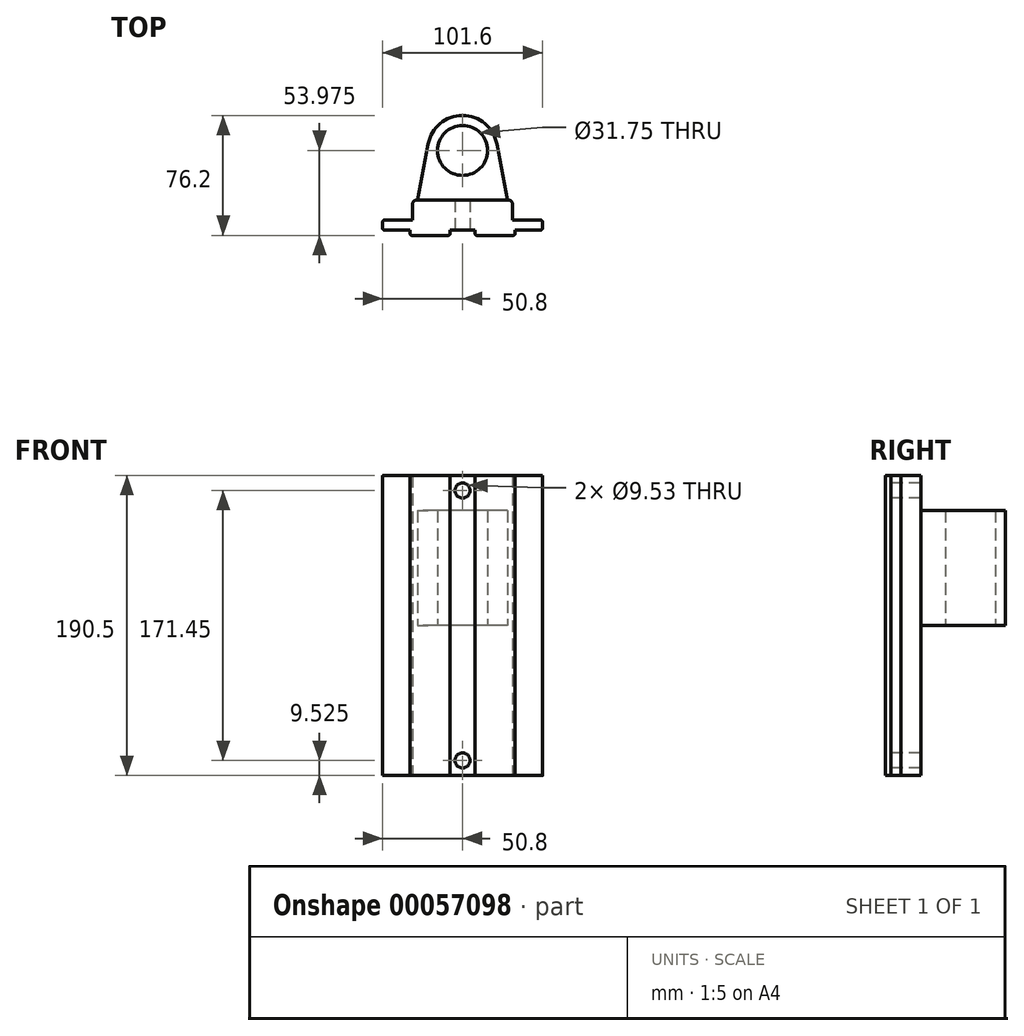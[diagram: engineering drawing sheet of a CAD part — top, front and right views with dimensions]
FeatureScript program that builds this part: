
annotation { "Feature Type Name" : "Feature", "Feature Type Description" : "" }
export const myFeature = defineFeature(function(context is Context, id is Id, definition is map)
    precondition{}
    {
        {
            var Q0;
            Q0=qCreatedBy(makeId("Top.planeOp"),FACE);
            var sketch = newSketch(context, id + "F0", { "sketchPlane" : qUnion([Q0])});
            skLineSegment(sketch, "E0", {"start": v(0, 0) * mm, "end": v(0, 22.42) * mm});
            skLineSegment(sketch, "E1", {"start": v(-9.2, 0) * mm, "end": v(-32.07, 0) * mm});
            skLineSegment(sketch, "E2", {"start": v(-50.8, 4.64) * mm, "end": v(-50.8, 8.45) * mm});
            skLineSegment(sketch, "E3", {"start": v(-49.53, 3.37) * mm, "end": v(0, 3.37) * mm});
            skLineSegment(sketch, "E4", {"start": v(-49.53, 9.72) * mm, "end": v(0, 9.72) * mm});
            skLineSegment(sketch, "E5", {"start": v(-33.34, 3.37) * mm, "end": v(-33.34, 1.27) * mm});
            skLineSegment(sketch, "E6", {"start": v(-7.94, 1.27) * mm, "end": v(-7.94, 3.37) * mm});
            skLineSegment(sketch, "E7", {"start": v(0, 22.42) * mm, "end": v(-29.21, 22.42) * mm});
            skLineSegment(sketch, "E8", {"start": v(-31.75, 19.88) * mm, "end": v(-31.75, 9.72) * mm});
            skPoint(sketch, "E9.visualSharp", {"position": v(-31.75, 22.42) * mm});
            skArc(sketch, "E9.filletArc", {"start": v(-29.21, 22.42) * mm, "mid": v(-31, 21.68) * mm, "end": v(-31.75, 19.88) * mm});
            skPoint(sketch, "E10.visualSharp", {"position": v(-50.8, 9.72) * mm});
            skArc(sketch, "E10.filletArc", {"start": v(-49.53, 9.72) * mm, "mid": v(-50.43, 9.35) * mm, "end": v(-50.8, 8.45) * mm});
            skPoint(sketch, "E11.visualSharp", {"position": v(-50.8, 3.37) * mm});
            skArc(sketch, "E11.filletArc", {"start": v(-50.8, 4.64) * mm, "mid": v(-50.43, 3.75) * mm, "end": v(-49.53, 3.37) * mm});
            skPoint(sketch, "E12.visualSharp", {"position": v(-33.34, 0) * mm});
            skArc(sketch, "E12.filletArc", {"start": v(-33.34, 1.27) * mm, "mid": v(-32.97, 0.37) * mm, "end": v(-32.07, 0) * mm});
            skPoint(sketch, "E13.visualSharp", {"position": v(-7.94, 0) * mm});
            skArc(sketch, "E13.filletArc", {"start": v(-9.2, 0) * mm, "mid": v(-8.3, 0.37) * mm, "end": v(-7.94, 1.27) * mm});
            skPoint(sketch, "E14.orphan", {"position": v(-26.99, 22.42) * mm});
            skArc(sketch, "E15.MirrorCS", {"start": v(49.53, 9.72) * mm, "mid": v(50.43, 9.35) * mm, "end": v(50.8, 8.45) * mm});
            skArc(sketch, "E16.MirrorCS", {"start": v(50.8, 4.64) * mm, "mid": v(50.43, 3.75) * mm, "end": v(49.53, 3.37) * mm});
            skLineSegment(sketch, "E17.MirrorCS", {"start": v(50.8, 4.64) * mm, "end": v(50.8, 8.45) * mm});
            skArc(sketch, "E18.MirrorCS", {"start": v(29.21, 22.42) * mm, "mid": v(31, 21.68) * mm, "end": v(31.75, 19.88) * mm});
            skArc(sketch, "E19.MirrorCS", {"start": v(33.34, 1.27) * mm, "mid": v(32.97, 0.37) * mm, "end": v(32.07, 0) * mm});
            skArc(sketch, "E20.MirrorCS", {"start": v(9.2, 0) * mm, "mid": v(8.3, 0.37) * mm, "end": v(7.94, 1.27) * mm});
            skLineSegment(sketch, "E21.MirrorCS", {"start": v(33.34, 3.37) * mm, "end": v(33.34, 1.27) * mm});
            skLineSegment(sketch, "E22.MirrorCS", {"start": v(7.94, 1.27) * mm, "end": v(7.94, 3.37) * mm});
            skPoint(sketch, "E23.MirrorP", {"position": v(50.8, 3.37) * mm});
            skLineSegment(sketch, "E24.MirrorCS", {"start": v(9.2, 0) * mm, "end": v(32.07, 0) * mm});
            skLineSegment(sketch, "E25.MirrorCS", {"start": v(49.53, 3.37) * mm, "end": v(0, 3.37) * mm});
            skLineSegment(sketch, "E26.MirrorCS", {"start": v(49.53, 9.72) * mm, "end": v(0, 9.72) * mm});
            skLineSegment(sketch, "E27.MirrorCS", {"start": v(0, 22.42) * mm, "end": v(29.21, 22.42) * mm});
            skLineSegment(sketch, "E28.MirrorCS", {"start": v(31.75, 19.88) * mm, "end": v(31.75, 9.72) * mm});
            skPoint(sketch, "E29.MirrorP", {"position": v(7.94, 0) * mm});
            skPoint(sketch, "E30.MirrorP", {"position": v(50.8, 9.72) * mm});
            skPoint(sketch, "E31.MirrorP", {"position": v(33.34, 0) * mm});
            skPoint(sketch, "E32.MirrorP", {"position": v(26.99, 22.42) * mm});
            skPoint(sketch, "E33.MirrorP", {"position": v(31.75, 22.42) * mm});
            skSolve(sketch);
        }
        {
            var Q0;
            Q0 = qSketchRegion(id + "F0", true);
            extrude(context, id + "F1", {"entities" : qUnion([Q0]), "depth" : 190.5 * mm});
        }
        {
            var Q0;
            Q0=qCreatedBy(makeId("Top.planeOp"),FACE);
            cPlane(context, id + "F2", {"entities" : qUnion([Q0]), "cplaneType" : CPlaneType.OFFSET, "offset" : 95.25 * mm, "width" : 152.4 * mm, "height" : 152.4 * mm});
        }
        {
            var Q0;
            Q0=qCreatedBy(id+"F2.planeOp",FACE);
            var sketch = newSketch(context, id + "F3", { "sketchPlane" : qUnion([Q0])});
            skLineSegment(sketch, "E34", {"start": v(-28.58, 22.22) * mm, "end": v(-21.84, 58.08) * mm});
            skLineSegment(sketch, "E35", {"start": v(0, 22.22) * mm, "end": v(0, 38.1) * mm});
            skPoint(sketch, "E36", {"position": v(-22.22, 53.98) * mm});
            skArc(sketch, "E37", {"start": v(0, 69.85) * mm, "mid": v(-15.88, 53.98) * mm, "end": v(0, 38.1) * mm});
            skArc(sketch, "E38", {"start": v(0, 76.2) * mm, "mid": v(-22.23, 53.98) * mm, "end": v(0, 31.75) * mm});
            skLineSegment(sketch, "E39", {"start": v(0, 76.2) * mm, "end": v(0, 69.85) * mm});
            skLineSegment(sketch, "E40", {"start": v(-28.58, 22.22) * mm, "end": v(0, 22.22) * mm});
            skLineSegment(sketch, "E41", {"start": v(0, 69.85) * mm, "end": v(0, 76.2) * mm});
            skPoint(sketch, "E42.orphan", {"position": v(0, 0) * mm});
            skPoint(sketch, "E43.MirrorP", {"position": v(22.22, 53.98) * mm});
            skLineSegment(sketch, "E44.MirrorCS", {"start": v(28.58, 22.22) * mm, "end": v(21.84, 58.08) * mm});
            skLineSegment(sketch, "E45.MirrorCS", {"start": v(28.58, 22.22) * mm, "end": v(0, 22.22) * mm});
            skArc(sketch, "E46.MirrorCS", {"start": v(0, 76.2) * mm, "mid": v(22.23, 53.98) * mm, "end": v(0, 31.75) * mm});
            skArc(sketch, "E47.MirrorCS", {"start": v(0, 69.85) * mm, "mid": v(15.88, 53.98) * mm, "end": v(0, 38.1) * mm});
            skSolve(sketch);
        }
        {
            var Q0;
            Q0 = qSketchRegion(id + "F3", true);
            extrude(context, id + "F4", {"entities" : qUnion([Q0]), "operationType" : NewBodyOperationType.ADD, "depth" : 73.02 * mm});
        }
        {
            var Q0;
            Q0=qCreatedBy(makeId("Front.planeOp"),FACE);
            var sketch = newSketch(context, id + "F5", { "sketchPlane" : qUnion([Q0])});
            skLineSegment(sketch, "E48", {"start": v(0, 0) * mm, "end": v(0, 225.44) * mm, "construction": true});
            skPoint(sketch, "E49", {"position": v(0, 9.53) * mm});
            skPoint(sketch, "E50", {"position": v(0, 180.98) * mm});
            skSolve(sketch);
        }
        {
            var Q0;
            Q0=sQuery(id+"F5.wireOp",VERTEX,"E50");
            var Q1;
            Q1=makeQuery(id+"F1.opExtrude","SWEPT_BODY",BODY,{"disambiguationData":[OSD([sQuery(id+"F0.wireOp",EDGE,"E1"),sQuery(id+"F0.wireOp",EDGE,"E2"),sQuery(id+"F0.wireOp",EDGE,"E3"),sQuery(id+"F0.wireOp",EDGE,"E4"),sQuery(id+"F0.wireOp",EDGE,"E5"),sQuery(id+"F0.wireOp",EDGE,"E6"),sQuery(id+"F0.wireOp",EDGE,"E7"),sQuery(id+"F0.wireOp",EDGE,"E8"),sQuery(id+"F0.wireOp",EDGE,"E9.filletArc"),sQuery(id+"F0.wireOp",EDGE,"E10.filletArc"),sQuery(id+"F0.wireOp",EDGE,"E11.filletArc"),sQuery(id+"F0.wireOp",EDGE,"E12.filletArc"),sQuery(id+"F0.wireOp",EDGE,"E13.filletArc"),sQuery(id+"F0.wireOp",EDGE,"E15.MirrorCS"),sQuery(id+"F0.wireOp",EDGE,"E16.MirrorCS"),sQuery(id+"F0.wireOp",EDGE,"E17.MirrorCS"),sQuery(id+"F0.wireOp",EDGE,"E18.MirrorCS"),sQuery(id+"F0.wireOp",EDGE,"E19.MirrorCS"),sQuery(id+"F0.wireOp",EDGE,"E20.MirrorCS"),sQuery(id+"F0.wireOp",EDGE,"E21.MirrorCS"),sQuery(id+"F0.wireOp",EDGE,"E22.MirrorCS"),sQuery(id+"F0.wireOp",EDGE,"E24.MirrorCS"),sQuery(id+"F0.wireOp",EDGE,"E25.MirrorCS"),sQuery(id+"F0.wireOp",EDGE,"E26.MirrorCS"),sQuery(id+"F0.wireOp",EDGE,"E27.MirrorCS"),sQuery(id+"F0.wireOp",EDGE,"E28.MirrorCS")])]});
            hole(context, id + "F6", {"style" : HoleStyle.SIMPLE, "holeDiameter" : 9.52 * mm, "endStyle" : HoleEndStyle.THROUGH, "locations" : qUnion([Q0]), "scope" : qUnion([Q1])});
        }
        {
            var Q0;
            Q0=sQuery(id+"F5.wireOp",VERTEX,"E49");
            var Q1;
            Q1=makeQuery(id+"F1.opExtrude","SWEPT_BODY",BODY,{"disambiguationData":[OSD([sQuery(id+"F0.wireOp",EDGE,"E1"),sQuery(id+"F0.wireOp",EDGE,"E2"),sQuery(id+"F0.wireOp",EDGE,"E3"),sQuery(id+"F0.wireOp",EDGE,"E4"),sQuery(id+"F0.wireOp",EDGE,"E5"),sQuery(id+"F0.wireOp",EDGE,"E6"),sQuery(id+"F0.wireOp",EDGE,"E7"),sQuery(id+"F0.wireOp",EDGE,"E8"),sQuery(id+"F0.wireOp",EDGE,"E9.filletArc"),sQuery(id+"F0.wireOp",EDGE,"E10.filletArc"),sQuery(id+"F0.wireOp",EDGE,"E11.filletArc"),sQuery(id+"F0.wireOp",EDGE,"E12.filletArc"),sQuery(id+"F0.wireOp",EDGE,"E13.filletArc"),sQuery(id+"F0.wireOp",EDGE,"E15.MirrorCS"),sQuery(id+"F0.wireOp",EDGE,"E16.MirrorCS"),sQuery(id+"F0.wireOp",EDGE,"E17.MirrorCS"),sQuery(id+"F0.wireOp",EDGE,"E18.MirrorCS"),sQuery(id+"F0.wireOp",EDGE,"E19.MirrorCS"),sQuery(id+"F0.wireOp",EDGE,"E20.MirrorCS"),sQuery(id+"F0.wireOp",EDGE,"E21.MirrorCS"),sQuery(id+"F0.wireOp",EDGE,"E22.MirrorCS"),sQuery(id+"F0.wireOp",EDGE,"E24.MirrorCS"),sQuery(id+"F0.wireOp",EDGE,"E25.MirrorCS"),sQuery(id+"F0.wireOp",EDGE,"E26.MirrorCS"),sQuery(id+"F0.wireOp",EDGE,"E27.MirrorCS"),sQuery(id+"F0.wireOp",EDGE,"E28.MirrorCS")])]});
            hole(context, id + "F7", {"style" : HoleStyle.SIMPLE, "holeDiameter" : 9.52 * mm, "endStyle" : HoleEndStyle.THROUGH, "locations" : qUnion([Q0]), "scope" : qUnion([Q1])});
        }
    });
